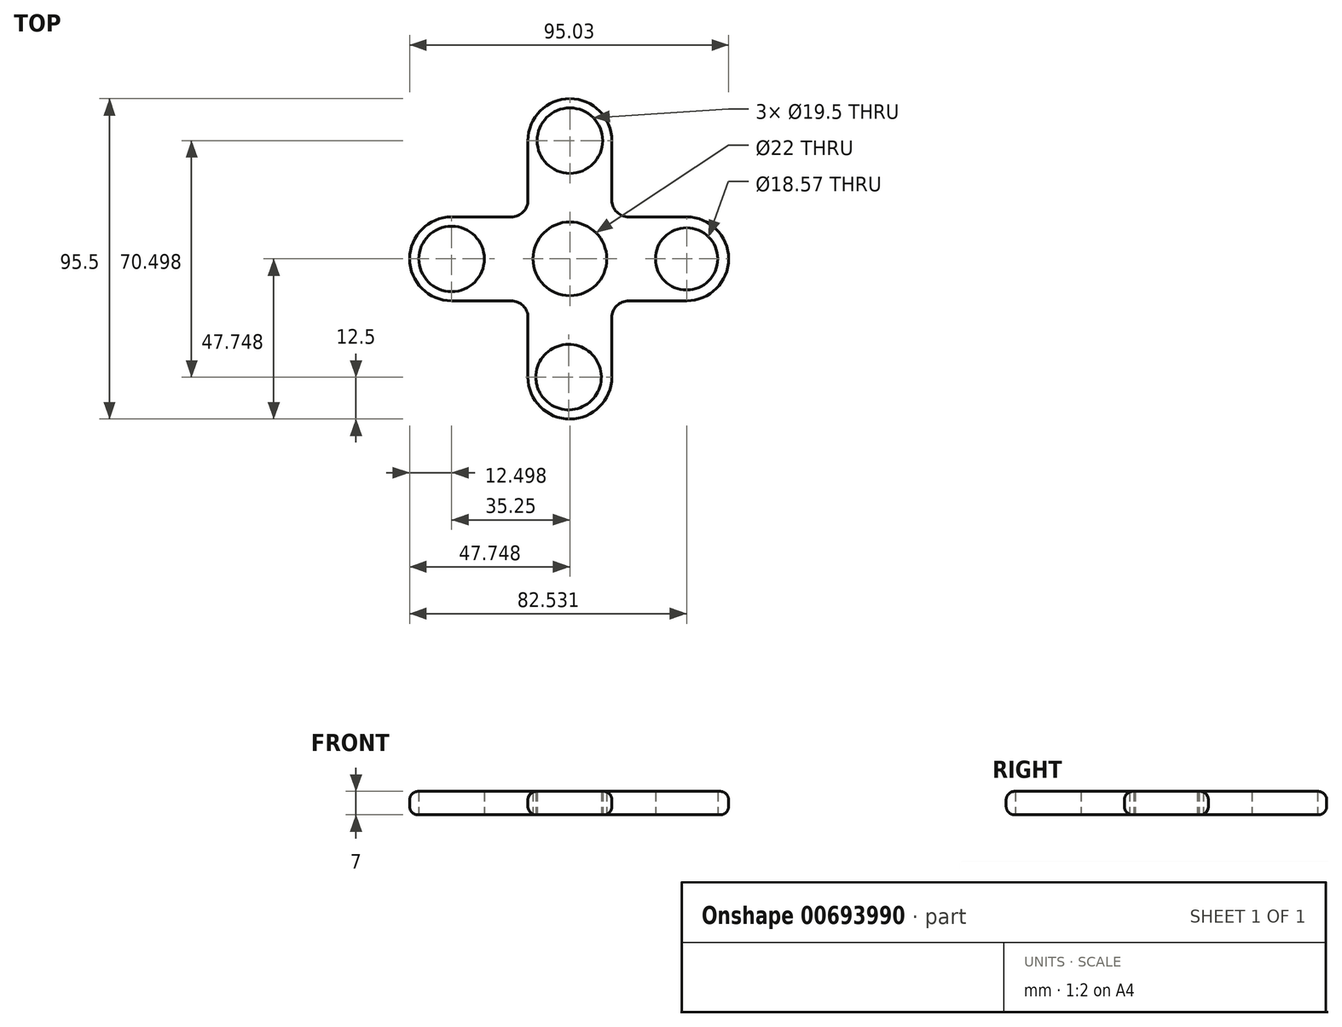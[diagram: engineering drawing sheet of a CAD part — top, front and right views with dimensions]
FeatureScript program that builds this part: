
annotation { "Feature Type Name" : "Feature", "Feature Type Description" : "" }
export const myFeature = defineFeature(function(context is Context, id is Id, definition is map)
    precondition{}
    {
        {
            var Q0;
            Q0=qCreatedBy(makeId("Top.planeOp"),FACE);
            var sketch = newSketch(context, id + "F0", { "sketchPlane" : qUnion([Q0])});
            skCircle(sketch, "E0", {"center": v(-111.62, 35.25) * mm, "radius": 11 * mm});
            skCircle(sketch, "E1", {"center": v(-112, 0) * mm, "radius": 9.75 * mm});
            skCircle(sketch, "E2", {"center": v(-111.62, 70.5) * mm, "radius": 9.75 * mm});
            skCircle(sketch, "E3", {"center": v(-76.84, 35.25) * mm, "radius": 9.28 * mm});
            skCircle(sketch, "E4", {"center": v(-146.87, 35.25) * mm, "radius": 9.75 * mm});
            skCircle(sketch, "E5", {"center": v(-111.62, 70.5) * mm, "radius": 12.5 * mm});
            skCircle(sketch, "E6", {"center": v(-146.87, 35.25) * mm, "radius": 12.5 * mm});
            skCircle(sketch, "E7", {"center": v(-111.62, 0) * mm, "radius": 12.5 * mm});
            skCircle(sketch, "E8", {"center": v(-76.84, 35.25) * mm, "radius": 12.5 * mm});
            skLineSegment(sketch, "E9.left", {"start": v(-124.12, 17.75) * mm, "end": v(-124.12, 0) * mm});
            skLineSegment(sketch, "E9.right", {"start": v(-99.12, 70.5) * mm, "end": v(-99.12, 52.75) * mm});
            skLineSegment(sketch, "E10.top", {"start": v(-94.12, 47.75) * mm, "end": v(-76.84, 47.75) * mm});
            skArc(sketch, "E11.filletArc", {"start": v(-99.12, 52.75) * mm, "mid": v(-97.66, 49.21) * mm, "end": v(-94.12, 47.75) * mm});
            skLineSegment(sketch, "E12", {"start": v(-146.87, 47.75) * mm, "end": v(-129.12, 47.75) * mm});
            skLineSegment(sketch, "E13", {"start": v(-124.12, 22.75) * mm, "end": v(-124.12, 0) * mm});
            skLineSegment(sketch, "E14", {"start": v(-99.12, 0) * mm, "end": v(-99.12, 17.75) * mm});
            skLineSegment(sketch, "E15", {"start": v(-94.12, 22.75) * mm, "end": v(-76.84, 22.75) * mm});
            skPoint(sketch, "E16.visualSharp", {"position": v(-99.12, 22.75) * mm});
            skArc(sketch, "E16.filletArc", {"start": v(-94.12, 22.75) * mm, "mid": v(-97.66, 21.28) * mm, "end": v(-99.12, 17.75) * mm});
            skArc(sketch, "E17.filletArc", {"start": v(-124.12, 17.75) * mm, "mid": v(-125.59, 21.28) * mm, "end": v(-129.12, 22.75) * mm});
            skLineSegment(sketch, "E18", {"start": v(-124.12, 70.5) * mm, "end": v(-124.12, 52.75) * mm});
            skPoint(sketch, "E19.visualSharp", {"position": v(-124.12, 47.75) * mm});
            skArc(sketch, "E19.filletArc", {"start": v(-129.12, 47.75) * mm, "mid": v(-125.59, 49.21) * mm, "end": v(-124.12, 52.75) * mm});
            skLineSegment(sketch, "E20", {"start": v(-129.12, 22.75) * mm, "end": v(-146.87, 22.75) * mm});
            skSolve(sketch);
        }
        {
            var Q0;
            Q0=makeQuery(id+"F0.imprint","IMPRINT",FACE,{"disambiguationData":[TD([[makeQuery(id+"F0.imprint","IMPRINT",EDGE,{"derivedFrom":sQuery(id+"F0.wireOp",EDGE,"E1")}),-1.0]])]});
            var Q1;
            Q1=makeQuery(id+"F0.imprint","IMPRINT",FACE,{"disambiguationData":[TD([[makeQuery(id+"F0.imprint","IMPRINT",EDGE,{"derivedFrom":sQuery(id+"F0.wireOp",EDGE,"E2")}),-1.0]])]});
            var Q2;
            Q2=makeQuery(id+"F0.imprint","IMPRINT",FACE,{"disambiguationData":[TD([[makeQuery(id+"F0.imprint","IMPRINT",EDGE,{"derivedFrom":sQuery(id+"F0.wireOp",EDGE,"E3")}),-1.0]])]});
            var Q3;
            Q3=makeQuery(id+"F0.imprint","IMPRINT",FACE,{"disambiguationData":[TD([[makeQuery(id+"F0.imprint","IMPRINT",EDGE,{"derivedFrom":sQuery(id+"F0.wireOp",EDGE,"E0")}),-1.0]])]});
            var Q4;
            Q4=makeQuery(id+"F0.imprint","IMPRINT",FACE,{"disambiguationData":[TD([[makeQuery(id+"F0.imprint","IMPRINT",EDGE,{"derivedFrom":sQuery(id+"F0.wireOp",EDGE,"E4")}),-1.0]])]});
            extrude(context, id + "F1", {"entities" : qUnion([Q0, Q1, Q2, Q3, Q4]), "depth" : 7 * mm, "offsetDistance" : 25 * mm});
        }
        {
            var Q0;
            Q0=makeQuery(id+"F1.opExtrude","CAP_EDGE",EDGE,{"disambiguationData":[OSD([sQuery(id+"F0.wireOp",EDGE,"E18")])],"isStart":false});
            var Q1;
            Q1=makeQuery(id+"F1.opExtrude","CAP_EDGE",EDGE,{"disambiguationData":[OSD([sQuery(id+"F0.wireOp",EDGE,"E19.filletArc")])],"isStart":false});
            var Q2;
            Q2=makeQuery(id+"F1.opExtrude","CAP_EDGE",EDGE,{"disambiguationData":[OSD([sQuery(id+"F0.wireOp",EDGE,"E20")])],"isStart":true});
            var Q3;
            Q3=makeQuery(id+"F1.opExtrude","CAP_EDGE",EDGE,{"disambiguationData":[OSD([sQuery(id+"F0.wireOp",EDGE,"E17.filletArc")])],"isStart":true});
            var Q4;
            Q4=makeQuery(id+"F1.opExtrude","CAP_EDGE",EDGE,{"disambiguationData":[OSD([sQuery(id+"F0.wireOp",EDGE,"E13")])],"isStart":true});
            var Q5;
            Q5=makeQuery(id+"F1.opExtrude","CAP_EDGE",EDGE,{"disambiguationData":[OSD([sQuery(id+"F0.wireOp",EDGE,"E7")])],"isStart":false});
            var Q6;
            Q6=makeQuery(id+"F1.opExtrude","CAP_EDGE",EDGE,{"disambiguationData":[OSD([sQuery(id+"F0.wireOp",EDGE,"E14")])],"isStart":true});
            var Q7;
            Q7=makeQuery(id+"F1.opExtrude","CAP_EDGE",EDGE,{"disambiguationData":[OSD([sQuery(id+"F0.wireOp",EDGE,"E7")])],"isStart":true});
            var Q8;
            Q8=makeQuery(id+"F1.opExtrude","CAP_EDGE",EDGE,{"disambiguationData":[OSD([sQuery(id+"F0.wireOp",EDGE,"E5")])],"isStart":false});
            var Q9;
            Q9=makeQuery(id+"F1.opExtrude","CAP_EDGE",EDGE,{"disambiguationData":[OSD([sQuery(id+"F0.wireOp",EDGE,"E9.right")])],"isStart":false});
            var Q10;
            Q10=makeQuery(id+"F1.opExtrude","CAP_EDGE",EDGE,{"disambiguationData":[OSD([sQuery(id+"F0.wireOp",EDGE,"E11.filletArc")])],"isStart":false});
            var Q11;
            Q11=makeQuery(id+"F1.opExtrude","CAP_EDGE",EDGE,{"disambiguationData":[OSD([sQuery(id+"F0.wireOp",EDGE,"E10.top")])],"isStart":false});
            var Q12;
            Q12=makeQuery(id+"F1.opExtrude","CAP_EDGE",EDGE,{"disambiguationData":[OSD([sQuery(id+"F0.wireOp",EDGE,"E8")])],"isStart":false});
            var Q13;
            Q13=makeQuery(id+"F1.opExtrude","CAP_EDGE",EDGE,{"disambiguationData":[OSD([sQuery(id+"F0.wireOp",EDGE,"E15")])],"isStart":false});
            var Q14;
            Q14=makeQuery(id+"F1.opExtrude","CAP_EDGE",EDGE,{"disambiguationData":[OSD([sQuery(id+"F0.wireOp",EDGE,"E16.filletArc")])],"isStart":false});
            var Q15;
            Q15=makeQuery(id+"F1.opExtrude","CAP_EDGE",EDGE,{"disambiguationData":[OSD([sQuery(id+"F0.wireOp",EDGE,"E14")])],"isStart":false});
            var Q16;
            Q16=makeQuery(id+"F1.opExtrude","CAP_EDGE",EDGE,{"disambiguationData":[OSD([sQuery(id+"F0.wireOp",EDGE,"E6")])],"isStart":false});
            var Q17;
            Q17=makeQuery(id+"F1.opExtrude","CAP_EDGE",EDGE,{"disambiguationData":[OSD([sQuery(id+"F0.wireOp",EDGE,"E12")])],"isStart":false});
            var Q18;
            Q18=makeQuery(id+"F1.opExtrude","CAP_EDGE",EDGE,{"disambiguationData":[OSD([sQuery(id+"F0.wireOp",EDGE,"E13")])],"isStart":false});
            var Q19;
            Q19=makeQuery(id+"F1.opExtrude","CAP_EDGE",EDGE,{"disambiguationData":[OSD([sQuery(id+"F0.wireOp",EDGE,"E17.filletArc")])],"isStart":false});
            var Q20;
            Q20=makeQuery(id+"F1.opExtrude","CAP_EDGE",EDGE,{"disambiguationData":[OSD([sQuery(id+"F0.wireOp",EDGE,"E20")])],"isStart":false});
            var Q21;
            Q21=makeQuery(id+"F1.opExtrude","CAP_EDGE",EDGE,{"disambiguationData":[OSD([sQuery(id+"F0.wireOp",EDGE,"E16.filletArc")])],"isStart":true});
            var Q22;
            Q22=makeQuery(id+"F1.opExtrude","CAP_EDGE",EDGE,{"disambiguationData":[OSD([sQuery(id+"F0.wireOp",EDGE,"E15")])],"isStart":true});
            var Q23;
            Q23=makeQuery(id+"F1.opExtrude","CAP_EDGE",EDGE,{"disambiguationData":[OSD([sQuery(id+"F0.wireOp",EDGE,"E8")])],"isStart":true});
            var Q24;
            Q24=makeQuery(id+"F1.opExtrude","CAP_EDGE",EDGE,{"disambiguationData":[OSD([sQuery(id+"F0.wireOp",EDGE,"E10.top")])],"isStart":true});
            var Q25;
            Q25=makeQuery(id+"F1.opExtrude","CAP_EDGE",EDGE,{"disambiguationData":[OSD([sQuery(id+"F0.wireOp",EDGE,"E5")])],"isStart":true});
            var Q26;
            Q26=makeQuery(id+"F1.opExtrude","CAP_EDGE",EDGE,{"disambiguationData":[OSD([sQuery(id+"F0.wireOp",EDGE,"E11.filletArc")])],"isStart":true});
            var Q27;
            Q27=makeQuery(id+"F1.opExtrude","CAP_EDGE",EDGE,{"disambiguationData":[OSD([sQuery(id+"F0.wireOp",EDGE,"E9.right")])],"isStart":true});
            var Q28;
            Q28=makeQuery(id+"F1.opExtrude","CAP_EDGE",EDGE,{"disambiguationData":[OSD([sQuery(id+"F0.wireOp",EDGE,"E18")])],"isStart":true});
            var Q29;
            Q29=makeQuery(id+"F1.opExtrude","CAP_EDGE",EDGE,{"disambiguationData":[OSD([sQuery(id+"F0.wireOp",EDGE,"E19.filletArc")])],"isStart":true});
            var Q30;
            Q30=makeQuery(id+"F1.opExtrude","CAP_EDGE",EDGE,{"disambiguationData":[OSD([sQuery(id+"F0.wireOp",EDGE,"E12")])],"isStart":true});
            var Q31;
            Q31=makeQuery(id+"F1.opExtrude","CAP_EDGE",EDGE,{"disambiguationData":[OSD([sQuery(id+"F0.wireOp",EDGE,"E6")])],"isStart":true});
            fillet(context, id + "F2", {"entities" : qUnion([Q0, Q1, Q2, Q3, Q4, Q5, Q6, Q7, Q8, Q9, Q10, Q11, Q12, Q13, Q14, Q15, Q16, Q17, Q18, Q19, Q20, Q21, Q22, Q23, Q24, Q25, Q26, Q27, Q28, Q29, Q30, Q31]), "radius" : 2.5 * mm, "tangentPropagation" : true, "allowEdgeOverflow" : false});
        }
    });
